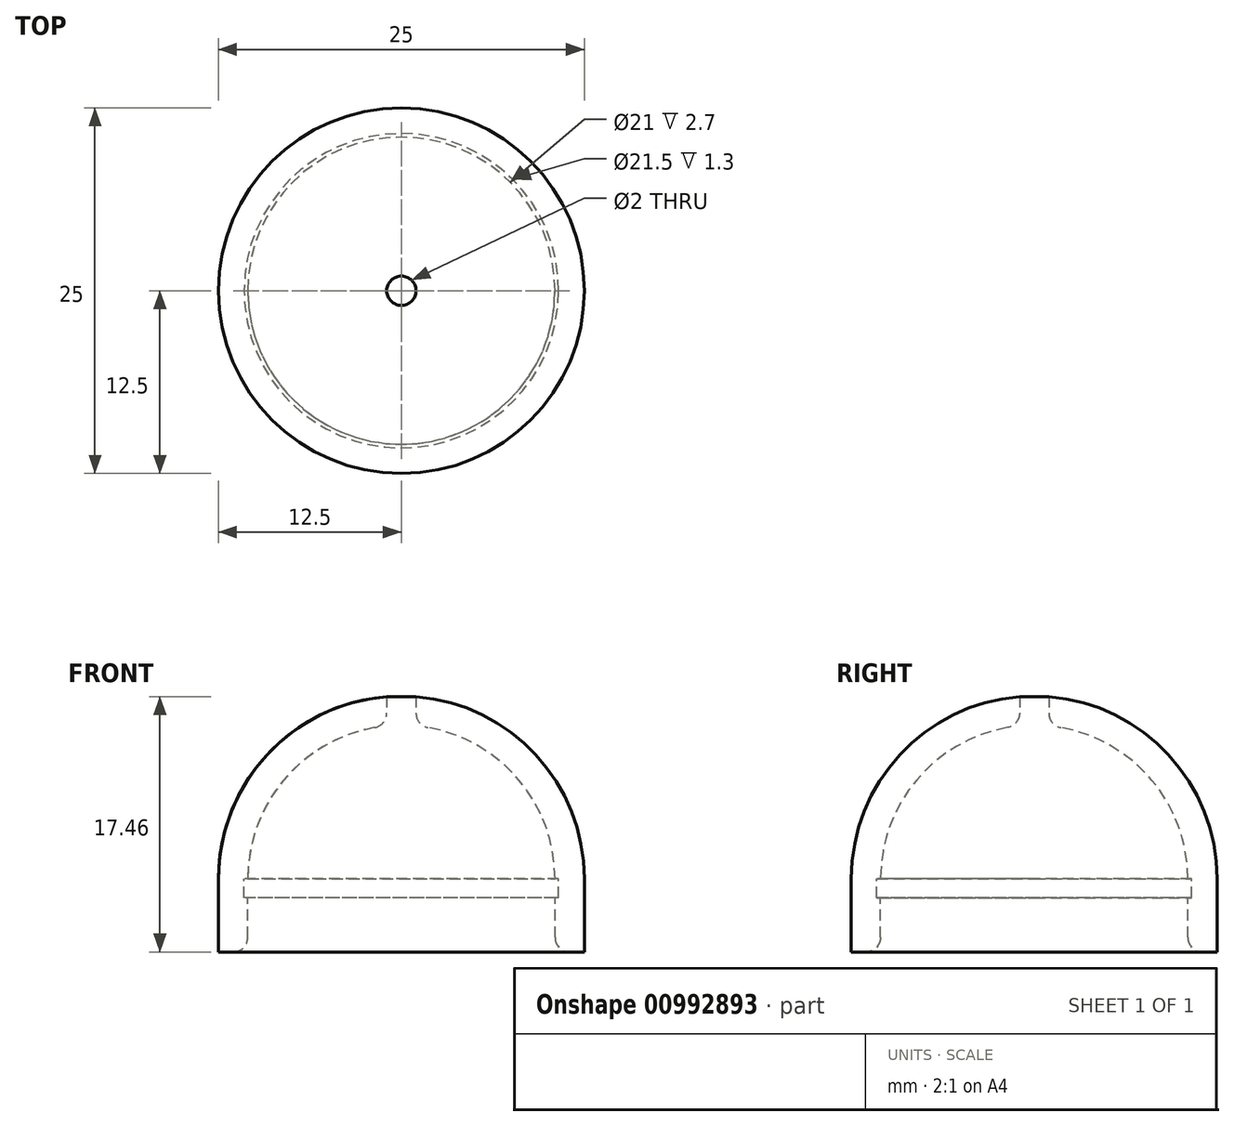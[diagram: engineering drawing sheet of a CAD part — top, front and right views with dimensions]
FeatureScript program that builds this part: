
annotation { "Feature Type Name" : "Feature", "Feature Type Description" : "" }
export const myFeature = defineFeature(function(context is Context, id is Id, definition is map)
    precondition{}
    {
        {
            var Q0;
            Q0=qCreatedBy(makeId("Front.planeOp"),FACE);
            var sketch = newSketch(context, id + "F0", { "sketchPlane" : qUnion([Q0])});
            skArc(sketch, "E0", {"start": v(0, 10.5) * mm, "mid": v(-7.42, 7.42) * mm, "end": v(-10.5, 0) * mm});
            skArc(sketch, "E1", {"start": v(0, 12.5) * mm, "mid": v(-8.84, 8.84) * mm, "end": v(-12.5, 0) * mm});
            skLineSegment(sketch, "E2", {"start": v(-10.5, 0) * mm, "end": v(-12.5, 0) * mm});
            skLineSegment(sketch, "E3", {"start": v(0, 10.5) * mm, "end": v(0, 12.5) * mm});
            skSolve(sketch);
        }
        {
            var Q0;
            Q0=qCreatedBy(makeId("Front.planeOp"),FACE);
            var sketch = newSketch(context, id + "F1", { "sketchPlane" : qUnion([Q0])});
            skLineSegment(sketch, "E4", {"start": v(0, 0) * mm, "end": v(0, 43.82) * mm});
            skSolve(sketch);
        }
        {
            var Q0;
            Q0=makeQuery(id+"F0.imprint","IMPRINT",FACE,{"disambiguationData":[TD([[makeQuery(id+"F0.imprint","IMPRINT",EDGE,{"derivedFrom":sQuery(id+"F0.wireOp",EDGE,"E0")}),-1.0]])]});
            var Q1;
            Q1=sQuery(id+"F1.wireOp",EDGE,"E4");
            revolve(context, id + "F2", {"entities" : qUnion([Q0]), "axis" : qUnion([Q1]), "revolveType" : RevolveType.FULL});
        }
        {
            var Q0;
            Q0=qCreatedBy(makeId("Top.planeOp"),FACE);
            var sketch = newSketch(context, id + "F3", { "sketchPlane" : qUnion([Q0])});
            skCircle(sketch, "E5", {"center": v(0, 0) * mm, "radius": 10.75 * mm});
            skSolve(sketch);
        }
        {
            var Q0;
            Q0=makeQuery(id+"F2.opRevolve","SWEPT_FACE",FACE,{"disambiguationData":[OSD([sQuery(id+"F0.wireOp",EDGE,"E2")])]});
            extrude(context, id + "F4", {"entities" : qUnion([Q0]), "operationType" : NewBodyOperationType.ADD, "depth" : 5 * mm});
        }
        {
            var Q0;
            Q0=qSketchRegion(id+"F3",true);
            extrude(context, id + "F5", {"entities" : qUnion([Q0]), "operationType" : NewBodyOperationType.REMOVE, "oppositeDirection" : true, "depth" : 1.3 * mm});
        }
        {
            var Q0;
            Q0=qCreatedBy(makeId("Top.planeOp"),FACE);
            var sketch = newSketch(context, id + "F6", { "sketchPlane" : qUnion([Q0])});
            skCircle(sketch, "E6", {"center": v(0, 0) * mm, "radius": 1 * mm});
            skSolve(sketch);
        }
        {
            var Q0;
            Q0=qSketchRegion(id+"F6",true);
            extrude(context, id + "F7", {"entities" : qUnion([Q0]), "operationType" : NewBodyOperationType.REMOVE, "depth" : 22.1 * mm});
        }
        {
            var Q0;
            Q0=makeQuery(id+"F4.opExtrude","CAP_EDGE",EDGE,{"disambiguationData":[OSD([sQuery(id+"F0.wireOp",EDGE,"E0"),sQuery(id+"F0.wireOp",EDGE,"E2")])],"isStart":false});
            var Q1;
            Q1=makeQuery(id+"F7.boolean.opBoolean","INTERSECT",EDGE,{"derivedFrom":[makeQuery(id+"F2.opRevolve","SWEPT_FACE",FACE,{"disambiguationData":[OSD([sQuery(id+"F0.wireOp",EDGE,"E0")])]}),makeQuery(id+"F7.opExtrude","SWEPT_FACE",FACE,{"disambiguationData":[OSD([sQuery(id+"F6.wireOp",EDGE,"E6")])]})]});
            fillet(context, id + "F8", {"entities" : qUnion([Q0, Q1]), "radius" : 1 * mm, "tangentPropagation" : true, "allowEdgeOverflow" : false});
        }
    });
